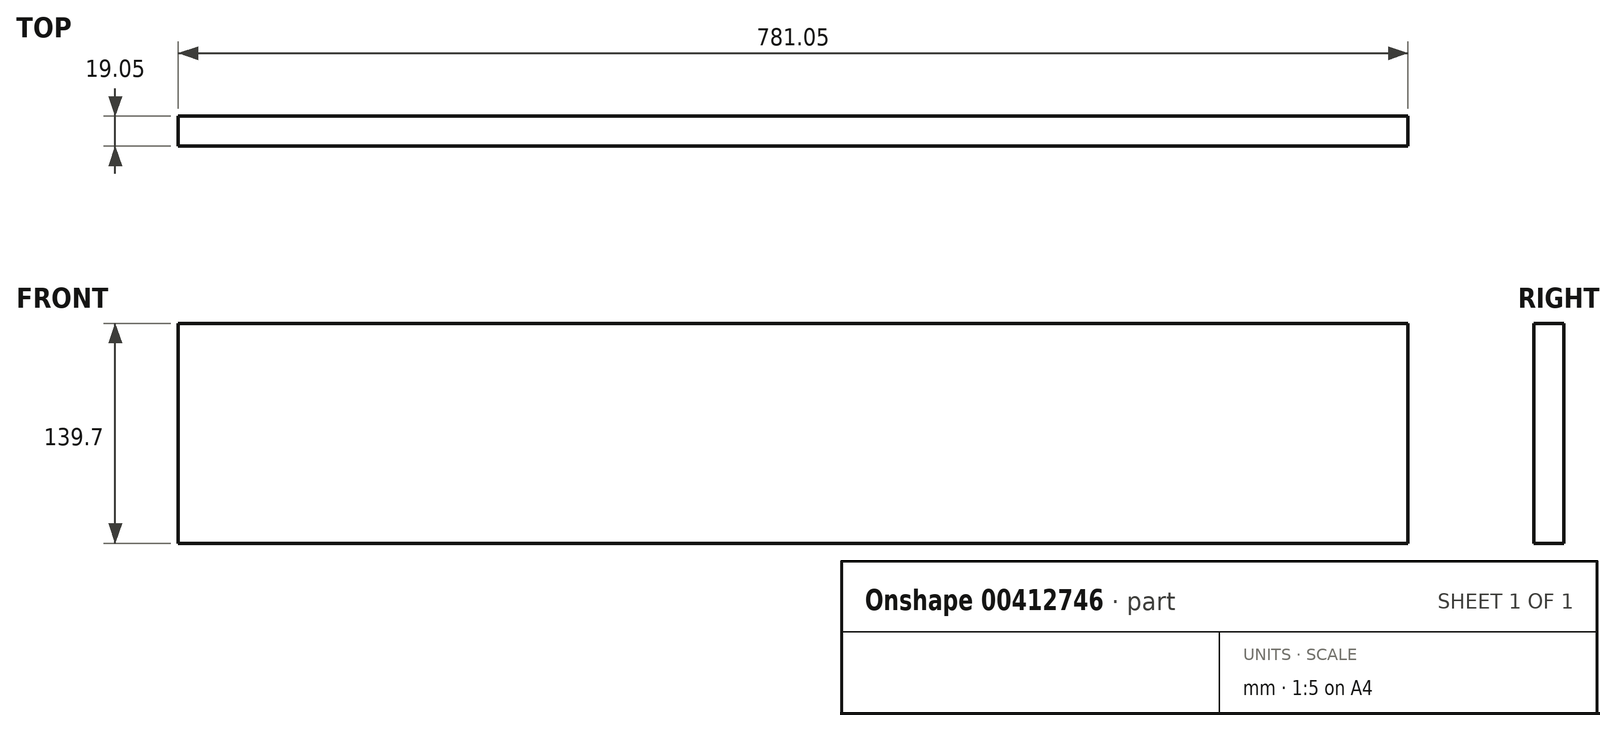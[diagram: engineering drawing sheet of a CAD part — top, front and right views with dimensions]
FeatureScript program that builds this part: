
annotation { "Feature Type Name" : "Feature", "Feature Type Description" : "" }
export const myFeature = defineFeature(function(context is Context, id is Id, definition is map)
    precondition{}
    {
        {
            var Q0;
            Q0=qCreatedBy(makeId("Front.planeOp"),FACE);
            var sketch = newSketch(context, id + "F0", { "sketchPlane" : qUnion([Q0])});
            skLineSegment(sketch, "E0.bottom", {"start": v(0, 0) * mm, "end": v(781.05, 0) * mm});
            skLineSegment(sketch, "E0.top", {"start": v(0, 139.7) * mm, "end": v(781.05, 139.7) * mm});
            skLineSegment(sketch, "E0.left", {"start": v(0, 0) * mm, "end": v(0, 139.7) * mm});
            skLineSegment(sketch, "E0.right", {"start": v(781.05, 0) * mm, "end": v(781.05, 139.7) * mm});
            skSolve(sketch);
        }
        {
            var Q0;
            Q0=makeQuery(id+"F0.imprint","IMPRINT",FACE,{"disambiguationData":[TD([[makeQuery(id+"F0.imprint","IMPRINT",EDGE,{"derivedFrom":sQuery(id+"F0.wireOp",EDGE,"E0.bottom")}),1.0]])]});
            extrude(context, id + "F1", {"entities" : qUnion([Q0]), "oppositeDirection" : true, "depth" : 19.05 * mm});
        }
    });
